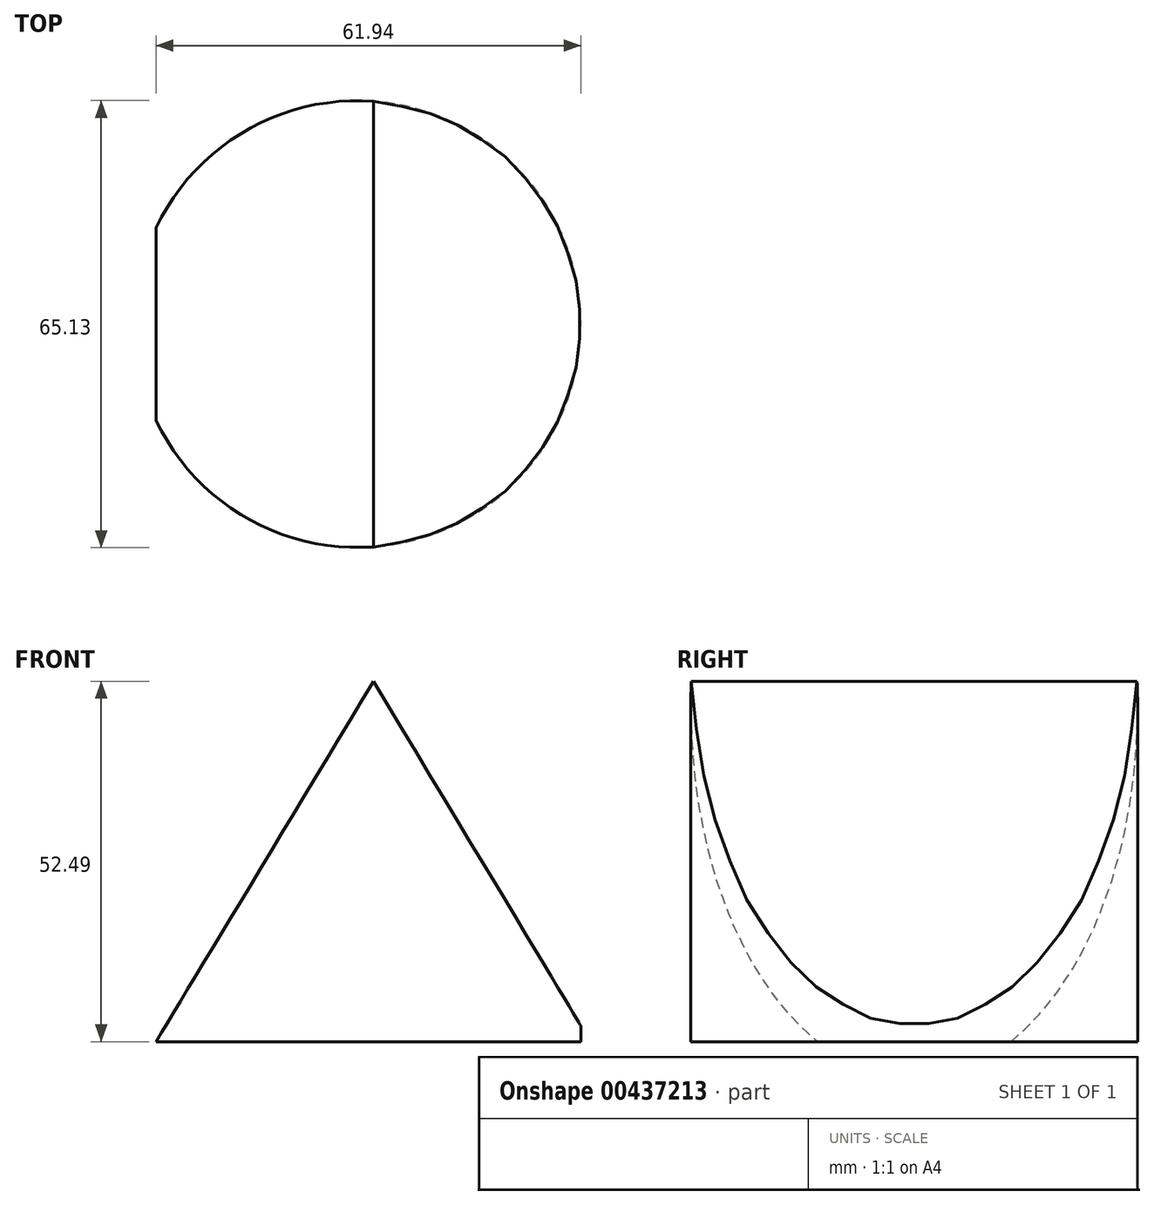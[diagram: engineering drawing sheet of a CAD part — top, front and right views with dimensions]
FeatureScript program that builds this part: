
annotation { "Feature Type Name" : "Feature", "Feature Type Description" : "" }
export const myFeature = defineFeature(function(context is Context, id is Id, definition is map)
    precondition{}
    {
        {
            var Q0;
            Q0=qCreatedBy(makeId("Top.planeOp"),FACE);
            var sketch = newSketch(context, id + "F0", { "sketchPlane" : qUnion([Q0])});
            skLineSegment(sketch, "E0.bottom", {"start": v(24.07, 13.85) * mm, "end": v(107.81, 13.85) * mm});
            skLineSegment(sketch, "E0.top", {"start": v(24.07, 98.98) * mm, "end": v(107.81, 98.98) * mm});
            skLineSegment(sketch, "E0.left", {"start": v(24.07, 13.85) * mm, "end": v(24.07, 98.98) * mm});
            skLineSegment(sketch, "E0.right", {"start": v(107.81, 13.85) * mm, "end": v(107.81, 98.98) * mm});
            skSolve(sketch);
        }
        {
            var Q0;
            Q0=makeQuery(id+"F0.imprint","IMPRINT",FACE,{"disambiguationData":[TD([[makeQuery(id+"F0.imprint","IMPRINT",EDGE,{"derivedFrom":sQuery(id+"F0.wireOp",EDGE,"E0.bottom")}),1.0]])]});
            extrude(context, id + "F1", {"entities" : qUnion([Q0]), "depth" : 76.2 * mm});
        }
        {
            var Q0;
            Q0=makeQuery(id+"F1.opExtrude","CAP_FACE",FACE,{"disambiguationData":[OSD([sQuery(id+"F0.wireOp",EDGE,"E0.bottom"),sQuery(id+"F0.wireOp",EDGE,"E0.top"),sQuery(id+"F0.wireOp",EDGE,"E0.left"),sQuery(id+"F0.wireOp",EDGE,"E0.right")])],"isStart":false});
            var sketch = newSketch(context, id + "F2", { "sketchPlane" : qUnion([Q0])});
            skCircle(sketch, "E1", {"center": v(64.77, 56.2) * mm, "radius": 32.57 * mm});
            skCircle(sketch, "E2", {"center": v(64.77, 56.2) * mm, "radius": 86.94 * mm});
            skSolve(sketch);
        }
        {
            var Q0;
            Q0=makeQuery(id+"F2.imprint","IMPRINT",FACE,{"disambiguationData":[TD([[makeQuery(id+"F2.imprint","IMPRINT",EDGE,{"derivedFrom":sQuery(id+"F2.wireOp",EDGE,"E1")}),-1.0]])]});
            extrude(context, id + "F3", {"entities" : qUnion([Q0]), "operationType" : NewBodyOperationType.REMOVE, "oppositeDirection" : true, "depth" : 76.2 * mm});
        }
        {
            var Q0;
            Q0=qCreatedBy(makeId("Front.planeOp"),FACE);
            var sketch = newSketch(context, id + "F4", { "sketchPlane" : qUnion([Q0])});
            skLineSegment(sketch, "E3", {"start": v(35.4, 0) * mm, "end": v(67.12, 52.49) * mm});
            skLineSegment(sketch, "E4", {"start": v(67.12, 52.49) * mm, "end": v(98.72, 0) * mm});
            skLineSegment(sketch, "E5", {"start": v(98.72, 0) * mm, "end": v(35.4, 0) * mm});
            skCircle(sketch, "E6", {"center": v(64.85, 15.61) * mm, "radius": 86.13 * mm});
            skSolve(sketch);
        }
        {
            var Q0;
            Q0=makeQuery(id+"F4.imprint","IMPRINT",FACE,{"disambiguationData":[TD([[makeQuery(id+"F4.imprint","IMPRINT",EDGE,{"derivedFrom":sQuery(id+"F4.wireOp",EDGE,"E3")}),1.0]])]});
            extrude(context, id + "F5", {"entities" : qUnion([Q0]), "operationType" : NewBodyOperationType.REMOVE, "oppositeDirection" : true, "depth" : 152.4 * mm});
        }
    });
